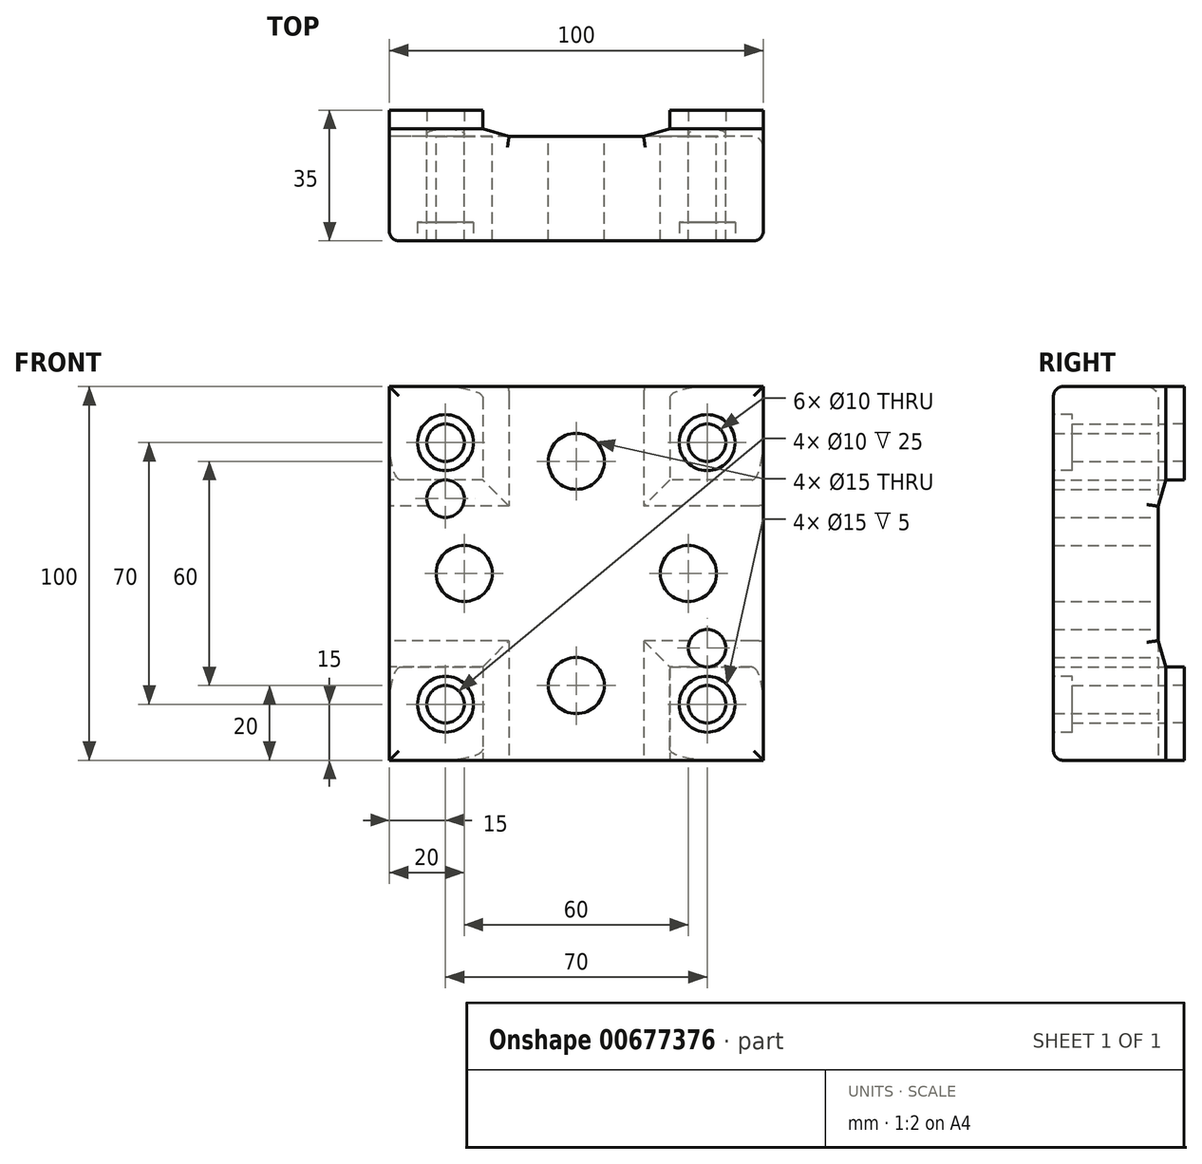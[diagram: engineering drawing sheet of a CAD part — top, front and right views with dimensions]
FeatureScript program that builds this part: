
annotation { "Feature Type Name" : "Feature", "Feature Type Description" : "" }
export const myFeature = defineFeature(function(context is Context, id is Id, definition is map)
    precondition{}
    {
        {
            var Q0;
            Q0=qCreatedBy(makeId("Front.planeOp"),FACE);
            var sketch = newSketch(context, id + "F0", { "sketchPlane" : qUnion([Q0])});
            skLineSegment(sketch, "E0.bottom", {"start": v(0, 0) * mm, "end": v(100, 0) * mm});
            skLineSegment(sketch, "E0.top", {"start": v(0, -100) * mm, "end": v(100, -100) * mm});
            skLineSegment(sketch, "E0.left", {"start": v(0, 0) * mm, "end": v(0, -100) * mm});
            skLineSegment(sketch, "E0.right", {"start": v(100, 0) * mm, "end": v(100, -100) * mm});
            skCircle(sketch, "E1", {"center": v(50, -20) * mm, "radius": 7.5 * mm});
            skCircle(sketch, "E2.1.0", {"center": v(20, -50) * mm, "radius": 7.5 * mm});
            skCircle(sketch, "E2.2.0", {"center": v(50, -80) * mm, "radius": 7.5 * mm});
            skCircle(sketch, "E2.3.0", {"center": v(80, -50) * mm, "radius": 7.5 * mm});
            skPoint(sketch, "E2.center", {"position": v(50, -50) * mm});
            skCircle(sketch, "E3", {"center": v(85, -15) * mm, "radius": 5 * mm});
            skCircle(sketch, "E4.1.0", {"center": v(15, -15) * mm, "radius": 5 * mm});
            skCircle(sketch, "E4.2.0", {"center": v(15, -85) * mm, "radius": 5 * mm});
            skCircle(sketch, "E4.3.0", {"center": v(85, -85) * mm, "radius": 5 * mm});
            skCircle(sketch, "E5", {"center": v(85, -70) * mm, "radius": 5 * mm});
            skCircle(sketch, "E6", {"center": v(15, -30) * mm, "radius": 5 * mm});
            skSolve(sketch);
        }
        {
            var Q0;
            Q0=qSketchRegion(id+"F0",true);
            extrude(context, id + "F1", {"entities" : qUnion([Q0]), "depth" : 30 * mm, "offsetDistance" : 25 * mm});
        }
        {
            var Q0;
            Q0=makeQuery(id+"F1.opExtrude","SWEPT_FACE",FACE,{"disambiguationData":[OSD([sQuery(id+"F0.wireOp",EDGE,"E0.top")])]});
            var sketch = newSketch(context, id + "F2", { "sketchPlane" : qUnion([Q0])});
            skLineSegment(sketch, "E7", {"start": v(25, 0) * mm, "end": v(32, 2) * mm});
            skLineSegment(sketch, "E8", {"start": v(32, 2) * mm, "end": v(68, 2) * mm});
            skLineSegment(sketch, "E9", {"start": v(68, 2) * mm, "end": v(75, 0) * mm});
            skLineSegment(sketch, "E10", {"start": v(25, 0) * mm, "end": v(75, 0) * mm});
            skSolve(sketch);
        }
        {
            var Q0;
            Q0=qSketchRegion(id+"F2",true);
            extrude(context, id + "F3", {"entities" : qUnion([Q0]), "operationType" : NewBodyOperationType.REMOVE, "endBound" : BoundingType.THROUGH_ALL, "oppositeDirection" : true, "depth" : 25 * mm, "offsetDistance" : 25 * mm});
        }
        {
            var Q0;
            Q0=makeQuery(id+"F1.opExtrude","SWEPT_FACE",FACE,{"disambiguationData":[OSD([sQuery(id+"F0.wireOp",EDGE,"E0.left")])]});
            var sketch = newSketch(context, id + "F4", { "sketchPlane" : qUnion([Q0])});
            skLineSegment(sketch, "E11", {"start": v(0, -25) * mm, "end": v(2, -32) * mm});
            skLineSegment(sketch, "E12", {"start": v(2, -32) * mm, "end": v(2, -68) * mm});
            skLineSegment(sketch, "E13", {"start": v(2, -68) * mm, "end": v(0, -75) * mm});
            skLineSegment(sketch, "E14", {"start": v(0, -25) * mm, "end": v(0, -75) * mm});
            skSolve(sketch);
        }
        {
            var Q0;
            Q0=qSketchRegion(id+"F4",true);
            extrude(context, id + "F5", {"entities" : qUnion([Q0]), "operationType" : NewBodyOperationType.REMOVE, "endBound" : BoundingType.THROUGH_ALL, "oppositeDirection" : true, "depth" : 25 * mm, "offsetDistance" : 25 * mm});
        }
        {
            var Q0;
            Q0=makeQuery(id+"F1.opExtrude","CAP_EDGE",EDGE,{"disambiguationData":[OSD([sQuery(id+"F0.wireOp",EDGE,"E0.right")])],"isStart":false});
            var Q1;
            Q1=makeQuery(id+"F1.opExtrude","CAP_EDGE",EDGE,{"disambiguationData":[OSD([sQuery(id+"F0.wireOp",EDGE,"E0.bottom")])],"isStart":false});
            var Q2;
            Q2=makeQuery(id+"F1.opExtrude","CAP_EDGE",EDGE,{"disambiguationData":[OSD([sQuery(id+"F0.wireOp",EDGE,"E0.left")])],"isStart":false});
            var Q3;
            Q3=makeQuery(id+"F1.opExtrude","CAP_EDGE",EDGE,{"disambiguationData":[OSD([sQuery(id+"F0.wireOp",EDGE,"E0.top")])],"isStart":false});
            fillet(context, id + "F6", {"entities" : qUnion([Q0, Q1, Q2, Q3]), "radius" : 2.5 * mm, "tangentPropagation" : true, "allowEdgeOverflow" : false});
        }
        {
            var Q0;
            Q0=makeQuery(id+"F5.boolean.opBoolean","INTERSECT",EDGE,{"derivedFrom":[makeQuery(id+"F1.opExtrude","SWEPT_FACE",FACE,{"disambiguationData":[OSD([sQuery(id+"F0.wireOp",EDGE,"E0.right")])]}),makeQuery(id+"F5.opExtrude","SWEPT_FACE",FACE,{"disambiguationData":[OSD([sQuery(id+"F4.wireOp",EDGE,"E12")])]})]});
            var Q1;
            Q1=makeQuery(id+"F5.boolean.opBoolean","INTERSECT",EDGE,{"derivedFrom":[makeQuery(id+"F1.opExtrude","SWEPT_FACE",FACE,{"disambiguationData":[OSD([sQuery(id+"F0.wireOp",EDGE,"E0.right")])]}),makeQuery(id+"F5.opExtrude","SWEPT_FACE",FACE,{"disambiguationData":[OSD([sQuery(id+"F4.wireOp",EDGE,"E11")])]})]});
            var Q2;
            Q2=makeQuery(id+"F5.boolean.opBoolean","INTERSECT",EDGE,{"derivedFrom":[makeQuery(id+"F1.opExtrude","SWEPT_FACE",FACE,{"disambiguationData":[OSD([sQuery(id+"F0.wireOp",EDGE,"E0.right")])]}),makeQuery(id+"F5.opExtrude","SWEPT_FACE",FACE,{"disambiguationData":[OSD([sQuery(id+"F4.wireOp",EDGE,"E13")])]})]});
            var Q3;
            Q3=makeQuery(id+"F5.boolean.opBoolean","COPY",EDGE,{"derivedFrom":makeQuery(id+"F5.opExtrude","CAP_EDGE",EDGE,{"disambiguationData":[OSD([sQuery(id+"F4.wireOp",EDGE,"E12")])],"isStart":true})});
            var Q4;
            Q4=makeQuery(id+"F5.boolean.opBoolean","COPY",EDGE,{"derivedFrom":makeQuery(id+"F5.opExtrude","CAP_EDGE",EDGE,{"disambiguationData":[OSD([sQuery(id+"F4.wireOp",EDGE,"E13")])],"isStart":true})});
            var Q5;
            Q5=makeQuery(id+"F5.boolean.opBoolean","COPY",EDGE,{"derivedFrom":makeQuery(id+"F5.opExtrude","CAP_EDGE",EDGE,{"disambiguationData":[OSD([sQuery(id+"F4.wireOp",EDGE,"E11")])],"isStart":true})});
            var Q6;
            Q6=makeQuery(id+"F3.boolean.opBoolean","COPY",EDGE,{"derivedFrom":makeQuery(id+"F3.opExtrude","CAP_EDGE",EDGE,{"disambiguationData":[OSD([sQuery(id+"F2.wireOp",EDGE,"E8")])],"isStart":true})});
            var Q7;
            Q7=makeQuery(id+"F3.boolean.opBoolean","COPY",EDGE,{"derivedFrom":makeQuery(id+"F3.opExtrude","CAP_EDGE",EDGE,{"disambiguationData":[OSD([sQuery(id+"F2.wireOp",EDGE,"E9")])],"isStart":true})});
            var Q8;
            Q8=makeQuery(id+"F3.boolean.opBoolean","COPY",EDGE,{"derivedFrom":makeQuery(id+"F3.opExtrude","CAP_EDGE",EDGE,{"disambiguationData":[OSD([sQuery(id+"F2.wireOp",EDGE,"E7")])],"isStart":true})});
            var Q9;
            Q9=makeQuery(id+"F3.boolean.opBoolean","INTERSECT",EDGE,{"derivedFrom":[makeQuery(id+"F1.opExtrude","SWEPT_FACE",FACE,{"disambiguationData":[OSD([sQuery(id+"F0.wireOp",EDGE,"E0.bottom")])]}),makeQuery(id+"F3.opExtrude","SWEPT_FACE",FACE,{"disambiguationData":[OSD([sQuery(id+"F2.wireOp",EDGE,"E8")])]})]});
            var Q10;
            Q10=makeQuery(id+"F3.boolean.opBoolean","INTERSECT",EDGE,{"derivedFrom":[makeQuery(id+"F1.opExtrude","SWEPT_FACE",FACE,{"disambiguationData":[OSD([sQuery(id+"F0.wireOp",EDGE,"E0.bottom")])]}),makeQuery(id+"F3.opExtrude","SWEPT_FACE",FACE,{"disambiguationData":[OSD([sQuery(id+"F2.wireOp",EDGE,"E9")])]})]});
            var Q11;
            Q11=makeQuery(id+"F3.boolean.opBoolean","INTERSECT",EDGE,{"derivedFrom":[makeQuery(id+"F1.opExtrude","SWEPT_FACE",FACE,{"disambiguationData":[OSD([sQuery(id+"F0.wireOp",EDGE,"E0.bottom")])]}),makeQuery(id+"F3.opExtrude","SWEPT_FACE",FACE,{"disambiguationData":[OSD([sQuery(id+"F2.wireOp",EDGE,"E7")])]})]});
            fillet(context, id + "F7", {"entities" : qUnion([Q0, Q1, Q2, Q3, Q4, Q5, Q6, Q7, Q8, Q9, Q10, Q11]), "radius" : 3 * mm, "tangentPropagation" : true, "allowEdgeOverflow" : false});
        }
        {
            var Q0;
            {var subQ1=sQuery(id+"F0.wireOp",EDGE,"E3");var subQ3=sQuery(id+"F0.wireOp",EDGE,"E0.right");var subQ4=makeQuery(id+"F1.opExtrude","SWEPT_FACE",FACE,{"disambiguationData":[OSD([subQ3])]});var subQ5=sQuery(id+"F0.wireOp",EDGE,"E0.bottom");var subQ6=makeQuery(id+"F1.opExtrude","SWEPT_FACE",FACE,{"disambiguationData":[OSD([subQ5])]});var subQ7=sQuery(id+"F0.wireOp",EDGE,"E2.3.0");var subQ8=sQuery(id+"F0.wireOp",EDGE,"E0.top");var subQ9=sQuery(id+"F0.wireOp",EDGE,"E5");var subQ10=sQuery(id+"F0.wireOp",EDGE,"E4.3.0");Q0=makeQuery(id+"F5.boolean.opBoolean","SPLIT",FACE,{"disambiguationData":[TD([subQ6])],"derivedFrom":makeQuery(id+"F3.boolean.opBoolean","SPLIT",FACE,{"disambiguationData":[TD([subQ4])],"derivedFrom":makeQuery(id+"F1.opExtrude","CAP_FACE",FACE,{"disambiguationData":[OSD([subQ5,subQ8,sQuery(id+"F0.wireOp",EDGE,"E0.left"),subQ3,sQuery(id+"F0.wireOp",EDGE,"E1"),sQuery(id+"F0.wireOp",EDGE,"E2.1.0"),sQuery(id+"F0.wireOp",EDGE,"E2.2.0"),subQ7,subQ1,sQuery(id+"F0.wireOp",EDGE,"E4.1.0"),sQuery(id+"F0.wireOp",EDGE,"E4.2.0"),subQ10,subQ9,sQuery(id+"F0.wireOp",EDGE,"E6")])],"isStart":true})})});}
            var sketch = newSketch(context, id + "F8", { "sketchPlane" : qUnion([Q0])});
            skLineSegment(sketch, "E15.0.0", {"start": v(-100, 0) * mm, "end": v(-100, -14.08) * mm});
            skEllipticalArc(sketch, "E15.0.1", {});
            skLineSegment(sketch, "E15.0.2", {"start": v(-97, -25) * mm, "end": v(-75, -25) * mm});
            skLineSegment(sketch, "E15.0.3", {"start": v(-75, -25) * mm, "end": v(-75, -3) * mm});
            skEllipticalArc(sketch, "E15.0.4", {});
            skLineSegment(sketch, "E15.0.5", {"start": v(-85.92, 0) * mm, "end": v(-100, 0) * mm});
            skCircle(sketch, "E16.0", {"center": v(-85, -15) * mm, "radius": 5 * mm});
            skLineSegment(sketch, "E17.0.0", {"start": v(-15, -25) * mm, "end": v(-3, -25) * mm});
            skEllipticalArc(sketch, "E17.0.1", {});
            skLineSegment(sketch, "E17.0.2", {"start": v(0, -14.08) * mm, "end": v(0, 0) * mm});
            skLineSegment(sketch, "E17.0.3", {"start": v(0, 0) * mm, "end": v(-14.08, 0) * mm});
            skEllipticalArc(sketch, "E17.0.4", {});
            skLineSegment(sketch, "E17.0.5", {"start": v(-25, -3) * mm, "end": v(-25, -25) * mm});
            skLineSegment(sketch, "E17.0.6", {"start": v(-25, -25) * mm, "end": v(-15, -25) * mm});
            skCircle(sketch, "E18.0", {"center": v(-15, -15) * mm, "radius": 5 * mm});
            skLineSegment(sketch, "E19.0.0", {"start": v(0, -100) * mm, "end": v(0, -85.92) * mm});
            skEllipticalArc(sketch, "E19.0.1", {});
            skLineSegment(sketch, "E19.0.2", {"start": v(-3, -75) * mm, "end": v(-25, -75) * mm});
            skLineSegment(sketch, "E19.0.3", {"start": v(-25, -75) * mm, "end": v(-25, -97) * mm});
            skEllipticalArc(sketch, "E19.0.4", {});
            skLineSegment(sketch, "E19.0.5", {"start": v(-14.08, -100) * mm, "end": v(0, -100) * mm});
            skCircle(sketch, "E20.0", {"center": v(-15, -85) * mm, "radius": 5 * mm});
            skLineSegment(sketch, "E21.0.0", {"start": v(-85, -75) * mm, "end": v(-97, -75) * mm});
            skEllipticalArc(sketch, "E21.0.1", {});
            skLineSegment(sketch, "E21.0.2", {"start": v(-100, -85.92) * mm, "end": v(-100, -100) * mm});
            skLineSegment(sketch, "E21.0.3", {"start": v(-100, -100) * mm, "end": v(-85.92, -100) * mm});
            skEllipticalArc(sketch, "E21.0.4", {});
            skLineSegment(sketch, "E21.0.5", {"start": v(-75, -97) * mm, "end": v(-75, -75) * mm});
            skLineSegment(sketch, "E21.0.6", {"start": v(-75, -75) * mm, "end": v(-85, -75) * mm});
            skCircle(sketch, "E22.0", {"center": v(-85, -85) * mm, "radius": 5 * mm});
            const initialGuessF8  = {"E15.0.1": [-0.097, -0.014079835166079229, 0, 1, 0.010920164833920783, 0.003, 1.5707963267948966, 3.141592653589793], "E15.0.4": [-0.08592016483392081, -0.003, 1, 0, 0.010920164833920783, 0.003, 0, 1.5707963267948966], "E17.0.1": [-0.003, -0.014079835166079236, 0, 1, 0.010920164833920783, 0.003, 3.141592653589793, 4.71238898038469], "E17.0.4": [-0.014079835166079243, -0.003, 1, 0, 0.010920164833920765, 0.003, 1.5707963267948966, 3.141592653589793], "E19.0.1": [-0.003, -0.08592016483392084, 0, 1, 0.010920164833920795, 0.003, 4.71238898038469, 0], "E19.0.4": [-0.014079835166079243, -0.097, 1, 0, 0.010920164833920765, 0.003, 3.141592653589793, 4.71238898038469], "E21.0.1": [-0.097, -0.08592016483392084, 0, 1, 0.010920164833920795, 0.003, 0, 1.5707963267948966], "E21.0.4": [-0.08592016483392081, -0.097, 1, 0, 0.010920164833920783, 0.003, 4.71238898038469, 0]};
            skSetInitialGuess(sketch, initialGuessF8);
            skSolve(sketch);
        }
        {
            var Q0;
            Q0=qSketchRegion(id+"F8",true);
            extrude(context, id + "F9", {"entities" : qUnion([Q0]), "depth" : 5 * mm, "offsetDistance" : 25 * mm});
        }
        {
            var Q0;
            Q0=makeQuery(id+"F1.opExtrude","CAP_FACE",FACE,{"disambiguationData":[OSD([sQuery(id+"F0.wireOp",EDGE,"E0.bottom"),sQuery(id+"F0.wireOp",EDGE,"E0.top"),sQuery(id+"F0.wireOp",EDGE,"E0.left"),sQuery(id+"F0.wireOp",EDGE,"E0.right"),sQuery(id+"F0.wireOp",EDGE,"E1"),sQuery(id+"F0.wireOp",EDGE,"E2.1.0"),sQuery(id+"F0.wireOp",EDGE,"E2.2.0"),sQuery(id+"F0.wireOp",EDGE,"E2.3.0"),sQuery(id+"F0.wireOp",EDGE,"E3"),sQuery(id+"F0.wireOp",EDGE,"E4.1.0"),sQuery(id+"F0.wireOp",EDGE,"E4.2.0"),sQuery(id+"F0.wireOp",EDGE,"E4.3.0"),sQuery(id+"F0.wireOp",EDGE,"E5"),sQuery(id+"F0.wireOp",EDGE,"E6")])],"isStart":false});
            var sketch = newSketch(context, id + "F10", { "sketchPlane" : qUnion([Q0])});
            skCircle(sketch, "E23.0", {"center": v(15, -15) * mm, "radius": 5 * mm});
            skCircle(sketch, "E24.0", {"center": v(85, -15) * mm, "radius": 5 * mm});
            skCircle(sketch, "E25.0", {"center": v(85, -85) * mm, "radius": 5 * mm});
            skCircle(sketch, "E26.0", {"center": v(15, -85) * mm, "radius": 5 * mm});
            skCircle(sketch, "E27", {"center": v(15, -85) * mm, "radius": 7.5 * mm});
            skCircle(sketch, "E28.1.0", {"center": v(85, -85) * mm, "radius": 7.5 * mm});
            skCircle(sketch, "E28.2.0", {"center": v(85, -15) * mm, "radius": 7.5 * mm});
            skCircle(sketch, "E28.3.0", {"center": v(15, -15) * mm, "radius": 7.5 * mm});
            skPoint(sketch, "E28.center", {"position": v(50, -50) * mm});
            skSolve(sketch);
        }
        {
            var Q0;
            Q0 = qSketchRegion(id + "F10", true);
            extrude(context, id + "F11", {"entities" : qUnion([Q0]), "operationType" : NewBodyOperationType.REMOVE, "oppositeDirection" : true, "depth" : 5 * mm, "offsetDistance" : 25 * mm});
        }
    });
